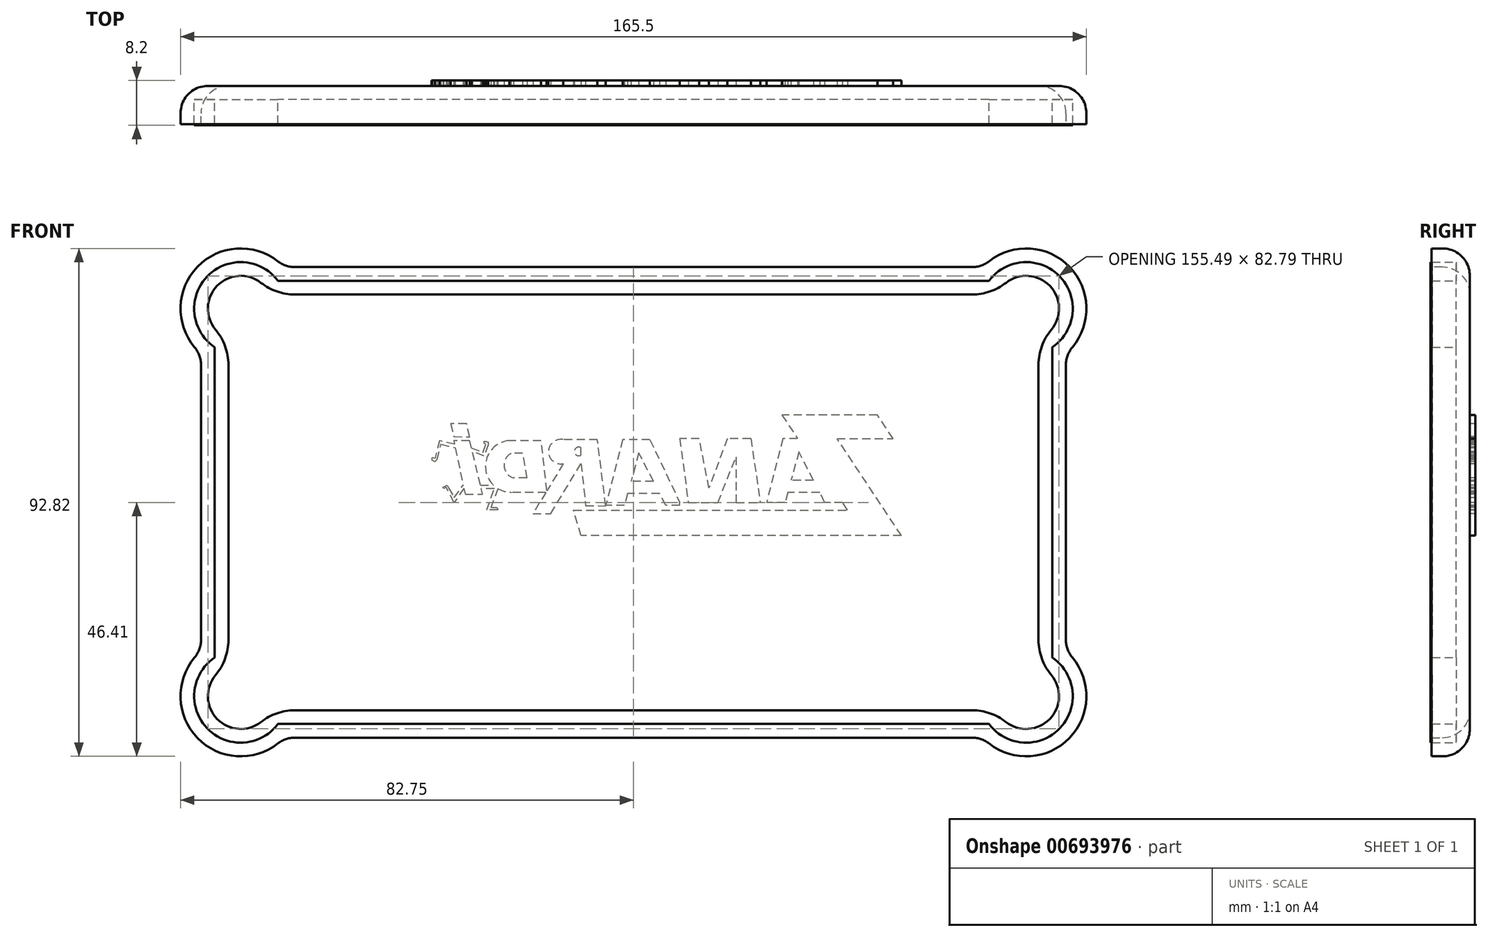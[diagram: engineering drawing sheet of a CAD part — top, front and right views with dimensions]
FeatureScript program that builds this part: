
annotation { "Feature Type Name" : "Feature", "Feature Type Description" : "" }
export const myFeature = defineFeature(function(context is Context, id is Id, definition is map)
    precondition{}
    {
        {
            var Q0;
            Q0=qCreatedBy(makeId("Front.planeOp"),FACE);
            var sketch = newSketch(context, id + "F0", { "sketchPlane" : qUnion([Q0])});
            skLineSegment(sketch, "E0.bottom", {"start": v(79, -43) * mm, "end": v(-79, -43) * mm});
            skLineSegment(sketch, "E0.top", {"start": v(79, 43) * mm, "end": v(-79, 43) * mm});
            skLineSegment(sketch, "E0.left", {"start": v(79, -43) * mm, "end": v(79, 43) * mm});
            skLineSegment(sketch, "E0.right", {"start": v(-79, -43) * mm, "end": v(-79, 43) * mm});
            skPoint(sketch, "E0.middle", {"position": v(0, 0) * mm});
            skArc(sketch, "E1", {"start": v(-79, 27.14) * mm, "mid": v(-79.69, 43.03) * mm, "end": v(-63.79, 43) * mm});
            skArc(sketch, "E2.MirrorCS", {"start": v(-79, -27.14) * mm, "mid": v(-79.69, -43.03) * mm, "end": v(-63.79, -43) * mm});
            skArc(sketch, "E3.MirrorCS", {"start": v(79, 27.14) * mm, "mid": v(79.69, 43.03) * mm, "end": v(63.79, 43) * mm});
            skArc(sketch, "E4.MirrorCS", {"start": v(79, -27.14) * mm, "mid": v(79.69, -43.03) * mm, "end": v(63.79, -43) * mm});
            skSolve(sketch);
        }
        {
            var Q0;
            Q0 = qSketchRegion(id + "F0", true);
            extrude(context, id + "F1", {"entities" : qUnion([Q0]), "depth" : 7 * mm, "offsetDistance" : 25 * mm});
        }
        {
            var Q0;
            Q0=makeQuery(id+"F1.opExtrude","CAP_FACE",FACE,{"disambiguationData":[OSD([sQuery(id+"F0.wireOp",EDGE,"E0.bottom"),sQuery(id+"F0.wireOp",EDGE,"E0.top"),sQuery(id+"F0.wireOp",EDGE,"E0.left"),sQuery(id+"F0.wireOp",EDGE,"E0.right")])],"isStart":false});
            shell(context, id + "F2", {"entities" : qUnion([Q0]), "thickness" : 2.5 * mm});
        }
        {
            var Q0;
            Q0=makeQuery(id+"F1.opExtrude","CAP_FACE",FACE,{"disambiguationData":[OSD([sQuery(id+"F0.wireOp",EDGE,"E0.bottom"),sQuery(id+"F0.wireOp",EDGE,"E0.top"),sQuery(id+"F0.wireOp",EDGE,"E0.left"),sQuery(id+"F0.wireOp",EDGE,"E0.right")])],"isStart":true});
            var Q1;
            Q1=makeQuery(id+"F1.opExtrude","SWEPT_EDGE",EDGE,{"disambiguationData":[OSD([sQuery(id+"F0.wireOp",EDGE,"E0.top"),sQuery(id+"F0.wireOp",EDGE,"E0.right")])]});
            var Q2;
            Q2=makeQuery(id+"F1.opExtrude","SWEPT_EDGE",EDGE,{"disambiguationData":[OSD([sQuery(id+"F0.wireOp",EDGE,"E0.bottom"),sQuery(id+"F0.wireOp",EDGE,"E0.right")])]});
            var Q3;
            Q3=makeQuery(id+"F1.opExtrude","SWEPT_EDGE",EDGE,{"disambiguationData":[OSD([sQuery(id+"F0.wireOp",EDGE,"E0.bottom"),sQuery(id+"F0.wireOp",EDGE,"E0.left")])]});
            var Q4;
            Q4=makeQuery(id+"F1.opExtrude","SWEPT_EDGE",EDGE,{"disambiguationData":[OSD([sQuery(id+"F0.wireOp",EDGE,"E0.top"),sQuery(id+"F0.wireOp",EDGE,"E0.left")])]});
            fillet(context, id + "F3", {"entities" : qUnion([Q0, Q1, Q2, Q3, Q4]), "radius" : 5 * mm, "tangentPropagation" : true, "allowEdgeOverflow" : false});
        }
        {
            var Q0;
            Q0=makeQuery(id+"F2.opShell","OFFSET_FACE",FACE,{"disambiguationData":[OSD([sQuery(id+"F0.wireOp",EDGE,"E0.bottom"),sQuery(id+"F0.wireOp",EDGE,"E0.top"),sQuery(id+"F0.wireOp",EDGE,"E0.left"),sQuery(id+"F0.wireOp",EDGE,"E0.right"),sQuery(id+"F0.wireOp",EDGE,"E1"),sQuery(id+"F0.wireOp",EDGE,"E2.MirrorCS"),sQuery(id+"F0.wireOp",EDGE,"E3.MirrorCS"),sQuery(id+"F0.wireOp",EDGE,"E4.MirrorCS")])]});
            extrude(context, id + "F4", {"entities" : qUnion([Q0]), "operationType" : NewBodyOperationType.ADD, "depth" : 4.7 * mm, "offsetDistance" : 25 * mm, "hasSecondDirection" : true, "secondDirectionOppositeDirection" : false, "secondDirectionDepth" : 4.4 * mm});
        }
        {
            var Q0;
            Q0=makeQuery(id+"F1.opExtrude","CAP_FACE",FACE,{"disambiguationData":[OSD([sQuery(id+"F0.wireOp",EDGE,"E0.bottom"),sQuery(id+"F0.wireOp",EDGE,"E0.top"),sQuery(id+"F0.wireOp",EDGE,"E0.left"),sQuery(id+"F0.wireOp",EDGE,"E0.right"),sQuery(id+"F0.wireOp",EDGE,"E1"),sQuery(id+"F0.wireOp",EDGE,"E2.MirrorCS"),sQuery(id+"F0.wireOp",EDGE,"E3.MirrorCS"),sQuery(id+"F0.wireOp",EDGE,"E4.MirrorCS")])],"isStart":true});
            extrude(context, id + "F5", {"entities" : qUnion([Q0]), "operationType" : NewBodyOperationType.REMOVE, "oppositeDirection" : true, "depth" : 23.4 * mm, "offsetDistance" : 25 * mm, "hasSecondDirection" : true, "secondDirectionOppositeDirection" : true, "secondDirectionDepth" : 6.4 * mm});
        }
        {
            var Q0;
            Q0=qCreatedBy(makeId("Front.planeOp"),FACE);
            var sketch = newSketch(context, id + "F6", { "sketchPlane" : qUnion([Q0])});
            skLineSegment(sketch, "E5", {"start": v(48.94, -6.1) * mm, "end": v(37.19, 11.64) * mm});
            skLineSegment(sketch, "E6", {"start": v(37.19, 11.64) * mm, "end": v(47.45, 11.64) * mm});
            skLineSegment(sketch, "E7", {"start": v(47.45, 11.64) * mm, "end": v(44.56, 16) * mm});
            skLineSegment(sketch, "E8", {"start": v(44.56, 16) * mm, "end": v(27.1, 16) * mm});
            skLineSegment(sketch, "E9", {"start": v(27.1, 16) * mm, "end": v(30, 11.64) * mm});
            skLineSegment(sketch, "E10", {"start": v(48.94, -6.1) * mm, "end": v(-9.56, -6.1) * mm});
            skLineSegment(sketch, "E11", {"start": v(-9.56, -6.1) * mm, "end": v(-10.96, -1.43) * mm});
            skLineSegment(sketch, "E12", {"start": v(-10.96, -1.43) * mm, "end": v(39.13, -1.43) * mm});
            skLineSegment(sketch, "E13", {"start": v(40.39, 0) * mm, "end": v(32.25, 11.64) * mm});
            skLineSegment(sketch, "E14", {"start": v(32.25, 11.64) * mm, "end": v(27.3, 11.64) * mm});
            skLineSegment(sketch, "E15", {"start": v(40.39, 0) * mm, "end": v(34.95, 0) * mm});
            skLineSegment(sketch, "E16", {"start": v(34.95, 0) * mm, "end": v(30.22, 9.24) * mm});
            skLineSegment(sketch, "E17", {"start": v(30.22, 9.24) * mm, "end": v(27.7, 0) * mm});
            skLineSegment(sketch, "E18", {"start": v(27.7, 0) * mm, "end": v(24.29, 0) * mm});
            skLineSegment(sketch, "E19", {"start": v(34.03, 1.8) * mm, "end": v(28.19, 1.8) * mm});
            skLineSegment(sketch, "E20", {"start": v(32.9, 4.01) * mm, "end": v(28.8, 4.01) * mm});
            skLineSegment(sketch, "E21", {"start": v(39.13, -1.43) * mm, "end": v(38.64, -0.67) * mm});
            skLineSegment(sketch, "E22", {"start": v(38.64, -0.67) * mm, "end": v(38.19, 0) * mm});
            skLineSegment(sketch, "E23", {"start": v(3.01, 11.44) * mm, "end": v(-1.95, 11.44) * mm});
            skLineSegment(sketch, "E24", {"start": v(11.06, -0.55) * mm, "end": v(5.88, -0.55) * mm});
            skLineSegment(sketch, "E25", {"start": v(5.88, -0.55) * mm, "end": v(0.98, 9.04) * mm});
            skLineSegment(sketch, "E26", {"start": v(0.98, 9.04) * mm, "end": v(-1.64, -0.55) * mm});
            skLineSegment(sketch, "E27", {"start": v(-1.64, -0.55) * mm, "end": v(-5.07, -0.55) * mm});
            skLineSegment(sketch, "E28", {"start": v(4.79, 1.6) * mm, "end": v(-1.05, 1.6) * mm});
            skLineSegment(sketch, "E29", {"start": v(3.65, 3.81) * mm, "end": v(-0.45, 3.81) * mm});
            skLineSegment(sketch, "E30", {"start": v(-6.58, 11.56) * mm, "end": v(-12.93, 11.56) * mm});
            skArc(sketch, "E31", {"start": v(-12.93, 11.56) * mm, "mid": v(-15.37, 8.9) * mm, "end": v(-12.52, 6.7) * mm});
            skLineSegment(sketch, "E32", {"start": v(-18.37, -1.98) * mm, "end": v(-14.65, -1.98) * mm});
            skLineSegment(sketch, "E33", {"start": v(-14.65, -1.98) * mm, "end": v(-9.56, 6.7) * mm});
            skLineSegment(sketch, "E34", {"start": v(-9.56, 6.7) * mm, "end": v(-8.74, -0.53) * mm});
            skLineSegment(sketch, "E35", {"start": v(-8.74, -0.53) * mm, "end": v(-5.07, -0.55) * mm});
            skLineSegment(sketch, "E36", {"start": v(-15.8, 1.84) * mm, "end": v(-16.86, 11.29) * mm});
            skLineSegment(sketch, "E37", {"start": v(-16.86, 11.29) * mm, "end": v(-22.7, 11.29) * mm});
            skLineSegment(sketch, "E38", {"start": v(-15.8, 1.84) * mm, "end": v(-22.31, 1.84) * mm});
            skArc(sketch, "E39", {"start": v(-22.7, 11.29) * mm, "mid": v(-27.04, 6.38) * mm, "end": v(-22.31, 1.84) * mm});
            skLineSegment(sketch, "E40", {"start": v(-19.45, 4.45) * mm, "end": v(-20.23, 8.97) * mm});
            skLineSegment(sketch, "E41", {"start": v(-20.23, 8.97) * mm, "end": v(-22.35, 8.97) * mm});
            skLineSegment(sketch, "E42", {"start": v(-19.45, 4.45) * mm, "end": v(-21.92, 4.45) * mm});
            skArc(sketch, "E43", {"start": v(-22.35, 8.97) * mm, "mid": v(-23.63, 6.57) * mm, "end": v(-21.92, 4.45) * mm});
            skLineSegment(sketch, "E44", {"start": v(-27.56, 1.48) * mm, "end": v(-29.91, 11.3) * mm});
            skLineSegment(sketch, "E45", {"start": v(-29.91, 11.3) * mm, "end": v(-32.83, 11.3) * mm});
            skLineSegment(sketch, "E46", {"start": v(-32.83, 11.3) * mm, "end": v(-30.75, 1.5) * mm});
            skLineSegment(sketch, "E47", {"start": v(-30.75, 1.5) * mm, "end": v(-27.56, 1.48) * mm});
            skLineSegment(sketch, "E48", {"start": v(-29.91, 11.95) * mm, "end": v(-30.5, 14.39) * mm});
            skLineSegment(sketch, "E49", {"start": v(-30.5, 14.39) * mm, "end": v(-33.4, 14.39) * mm});
            skLineSegment(sketch, "E50", {"start": v(-33.4, 14.39) * mm, "end": v(-32.83, 12) * mm});
            skLineSegment(sketch, "E51", {"start": v(-32.83, 12) * mm, "end": v(-29.91, 11.95) * mm});
            skLineSegment(sketch, "E52", {"start": v(-32.68, 10.62) * mm, "end": v(-35.44, 11.3) * mm});
            skLineSegment(sketch, "E53", {"start": v(-35.44, 11.3) * mm, "end": v(-36.24, 8.06) * mm});
            skLineSegment(sketch, "E54", {"start": v(-36.24, 8.06) * mm, "end": v(-36.76, 8.18) * mm});
            skLineSegment(sketch, "E55", {"start": v(-36.76, 8.18) * mm, "end": v(-36.86, 7.76) * mm});
            skLineSegment(sketch, "E56", {"start": v(-36.86, 7.76) * mm, "end": v(-36.24, 7.49) * mm});
            skLineSegment(sketch, "E57", {"start": v(-36.24, 7.49) * mm, "end": v(-35.88, 7.83) * mm});
            skLineSegment(sketch, "E58", {"start": v(-35.88, 7.83) * mm, "end": v(-35.15, 10.65) * mm});
            skLineSegment(sketch, "E59", {"start": v(-35.15, 10.65) * mm, "end": v(-32.55, 9.98) * mm});
            skLineSegment(sketch, "E60", {"start": v(-32.68, 10.62) * mm, "end": v(-32.37, 10.55) * mm});
            skArc(sketch, "E61", {"start": v(-32.55, 9.98) * mm, "mid": v(-32.15, 10.17) * mm, "end": v(-32.37, 10.55) * mm});
            skLineSegment(sketch, "E62", {"start": v(-29.59, 9.94) * mm, "end": v(-27.5, 9.14) * mm});
            skLineSegment(sketch, "E63", {"start": v(-27.5, 9.14) * mm, "end": v(-26.91, 10.66) * mm});
            skLineSegment(sketch, "E64", {"start": v(-26.91, 10.66) * mm, "end": v(-27.22, 10.78) * mm});
            skLineSegment(sketch, "E65", {"start": v(-27.22, 10.78) * mm, "end": v(-27.3, 11.13) * mm});
            skLineSegment(sketch, "E66", {"start": v(-27.3, 11.13) * mm, "end": v(-26.91, 11.13) * mm});
            skLineSegment(sketch, "E67", {"start": v(-26.91, 11.13) * mm, "end": v(-26.54, 10.99) * mm});
            skLineSegment(sketch, "E68", {"start": v(-26.54, 10.99) * mm, "end": v(-26.54, 10.5) * mm});
            skLineSegment(sketch, "E69", {"start": v(-26.54, 10.5) * mm, "end": v(-27.3, 8.49) * mm});
            skLineSegment(sketch, "E70", {"start": v(-27.3, 8.49) * mm, "end": v(-29.43, 9.3) * mm});
            skLineSegment(sketch, "E71", {"start": v(-30.98, 2.58) * mm, "end": v(-32.75, 0) * mm});
            skLineSegment(sketch, "E72", {"start": v(-32.75, 0) * mm, "end": v(-34.2, 2.76) * mm});
            skLineSegment(sketch, "E73", {"start": v(-34.2, 2.76) * mm, "end": v(-34.68, 2.52) * mm});
            skLineSegment(sketch, "E74", {"start": v(-34.68, 2.52) * mm, "end": v(-34.8, 2.76) * mm});
            skLineSegment(sketch, "E75", {"start": v(-34.8, 2.76) * mm, "end": v(-34.06, 3.16) * mm});
            skLineSegment(sketch, "E76", {"start": v(-34.06, 3.16) * mm, "end": v(-33.8, 2.65) * mm});
            skLineSegment(sketch, "E77", {"start": v(-33.8, 2.65) * mm, "end": v(-32.75, 0.85) * mm});
            skLineSegment(sketch, "E78", {"start": v(-32.75, 0.85) * mm, "end": v(-31.1, 3.16) * mm});
            skLineSegment(sketch, "E79", {"start": v(-27.96, 3.16) * mm, "end": v(-24.56, 3.13) * mm});
            skLineSegment(sketch, "E80", {"start": v(-24.56, 3.13) * mm, "end": v(-26.03, -0.9) * mm});
            skLineSegment(sketch, "E81", {"start": v(-26.03, -0.9) * mm, "end": v(-24.94, -0.9) * mm});
            skLineSegment(sketch, "E82", {"start": v(-24.94, -0.9) * mm, "end": v(-24.8, -1.37) * mm});
            skLineSegment(sketch, "E83", {"start": v(-24.8, -1.37) * mm, "end": v(-26.78, -1.37) * mm});
            skLineSegment(sketch, "E84", {"start": v(-26.78, -1.37) * mm, "end": v(-25.43, 2.52) * mm});
            skLineSegment(sketch, "E85", {"start": v(-25.43, 2.52) * mm, "end": v(-30.26, 2.52) * mm});
            skLineSegment(sketch, "E86", {"start": v(-27.96, 3.16) * mm, "end": v(-30.41, 3.16) * mm});
            skArc(sketch, "E87", {"start": v(-30.41, 3.16) * mm, "mid": v(-30.59, 2.78) * mm, "end": v(-30.26, 2.52) * mm});
            skLineSegment(sketch, "E88", {"start": v(-1.95, 11.44) * mm, "end": v(-5.07, -0.55) * mm});
            skLineSegment(sketch, "E89", {"start": v(-5.07, -0.55) * mm, "end": v(-6.58, 11.56) * mm});
            skLineSegment(sketch, "E90", {"start": v(3.01, 11.44) * mm, "end": v(8.47, 0) * mm});
            skLineSegment(sketch, "E91", {"start": v(27.3, 11.64) * mm, "end": v(24.29, 0) * mm});
            skLineSegment(sketch, "E92", {"start": v(-12.93, 6.7) * mm, "end": v(-14.78, 3.54) * mm});
            skLineSegment(sketch, "E93", {"start": v(-14.78, 3.54) * mm, "end": v(-15.65, 2.07) * mm});
            skLineSegment(sketch, "E94", {"start": v(-18.37, -1.98) * mm, "end": v(-15.87, 1.64) * mm});
            skLineSegment(sketch, "E95", {"start": v(8.47, -0.55) * mm, "end": v(8.47, 0) * mm});
            skLineSegment(sketch, "E96", {"start": v(22.55, 11.66) * mm, "end": v(18.26, 11.66) * mm});
            skLineSegment(sketch, "E97", {"start": v(18.26, 11.66) * mm, "end": v(14.9, 2.61) * mm});
            skLineSegment(sketch, "E98", {"start": v(14.9, 2.61) * mm, "end": v(13.13, 11.66) * mm});
            skLineSegment(sketch, "E99", {"start": v(13.13, 11.66) * mm, "end": v(9.58, 11.66) * mm});
            skLineSegment(sketch, "E100", {"start": v(9.58, 11.66) * mm, "end": v(11.12, 0) * mm});
            skLineSegment(sketch, "E101", {"start": v(11.12, 0) * mm, "end": v(16.53, 0) * mm});
            skLineSegment(sketch, "E102", {"start": v(16.53, 0) * mm, "end": v(19.84, 8.3) * mm});
            skLineSegment(sketch, "E103", {"start": v(19.84, 8.3) * mm, "end": v(19.84, 0) * mm});
            skPoint(sketch, "E104.endSnap0", {"position": v(8.47, -0.55) * mm});
            skLineSegment(sketch, "E105", {"start": v(22.55, 11.66) * mm, "end": v(24.29, 0) * mm});
            skLineSegment(sketch, "E106", {"start": v(11.12, 0) * mm, "end": v(11.06, -0.55) * mm});
            skLineSegment(sketch, "E107", {"start": v(19.84, 0) * mm, "end": v(23.37, 0) * mm});
            skSolve(sketch);
        }
        {
            var Q0;
            Q0=qCreatedBy(makeId("Front.planeOp"),FACE);
            var sketch = newSketch(context, id + "F7", { "sketchPlane" : qUnion([Q0])});
            skLineSegment(sketch, "E108", {"start": v(21.44, 11.66) * mm, "end": v(17.15, 11.66) * mm});
            skLineSegment(sketch, "E109", {"start": v(17.15, 11.66) * mm, "end": v(13.79, 2.61) * mm});
            skLineSegment(sketch, "E110", {"start": v(13.79, 2.61) * mm, "end": v(12.01, 11.66) * mm});
            skLineSegment(sketch, "E111", {"start": v(12.01, 11.66) * mm, "end": v(8.47, 11.66) * mm});
            skLineSegment(sketch, "E112", {"start": v(8.47, 11.66) * mm, "end": v(10, 0) * mm});
            skLineSegment(sketch, "E113", {"start": v(10, 0) * mm, "end": v(15.42, 0) * mm});
            skLineSegment(sketch, "E114", {"start": v(15.42, 0) * mm, "end": v(18.73, 8.3) * mm});
            skLineSegment(sketch, "E115", {"start": v(18.73, 8.3) * mm, "end": v(18.73, 0) * mm});
            skLineSegment(sketch, "E116", {"start": v(21.44, 11.66) * mm, "end": v(23.18, 0) * mm});
            skLineSegment(sketch, "E117", {"start": v(18.73, 0) * mm, "end": v(23.18, 0) * mm});
            skLineSegment(sketch, "E118", {"start": v(-6.58, 11.47) * mm, "end": v(-12.81, 11.47) * mm});
            skLineSegment(sketch, "E119", {"start": v(-18.38, -2.07) * mm, "end": v(-15.14, -2.07) * mm});
            skLineSegment(sketch, "E120", {"start": v(-15.14, -2.07) * mm, "end": v(-9.56, 7.08) * mm});
            skLineSegment(sketch, "E121", {"start": v(-9.56, 7.08) * mm, "end": v(-8.75, -0.62) * mm});
            skLineSegment(sketch, "E122", {"start": v(-8.75, -0.62) * mm, "end": v(-5.07, -0.64) * mm});
            skLineSegment(sketch, "E123", {"start": v(-9.56, 8.64) * mm, "end": v(-9.56, 9.97) * mm});
            skArc(sketch, "E124", {"start": v(-9.56, 9.97) * mm, "mid": v(-10.8, 9.3) * mm, "end": v(-9.56, 8.64) * mm});
            skLineSegment(sketch, "E125", {"start": v(-5.07, -0.64) * mm, "end": v(-6.58, 11.47) * mm});
            skLineSegment(sketch, "E126", {"start": v(-12.8, 7.08) * mm, "end": v(-18.38, -2.07) * mm});
            skArc(sketch, "E127", {"start": v(-12.81, 11.47) * mm, "mid": v(-15.53, 9.27) * mm, "end": v(-12.8, 7.08) * mm});
            skSolve(sketch);
        }
        {
            var Q0;
            Q0 = qSketchRegion(id + "F7", true);
            extrude(context, id + "F8", {"entities" : qUnion([Q0]), "operationType" : NewBodyOperationType.ADD, "oppositeDirection" : true, "depth" : 1 * mm, "offsetDistance" : 25 * mm});
        }
        {
            var Q0;
            Q0 = qSketchRegion(id + "F6", true);
            extrude(context, id + "F9", {"entities" : qUnion([Q0]), "operationType" : NewBodyOperationType.ADD, "oppositeDirection" : true, "depth" : 1 * mm, "offsetDistance" : 25 * mm});
        }
    });
